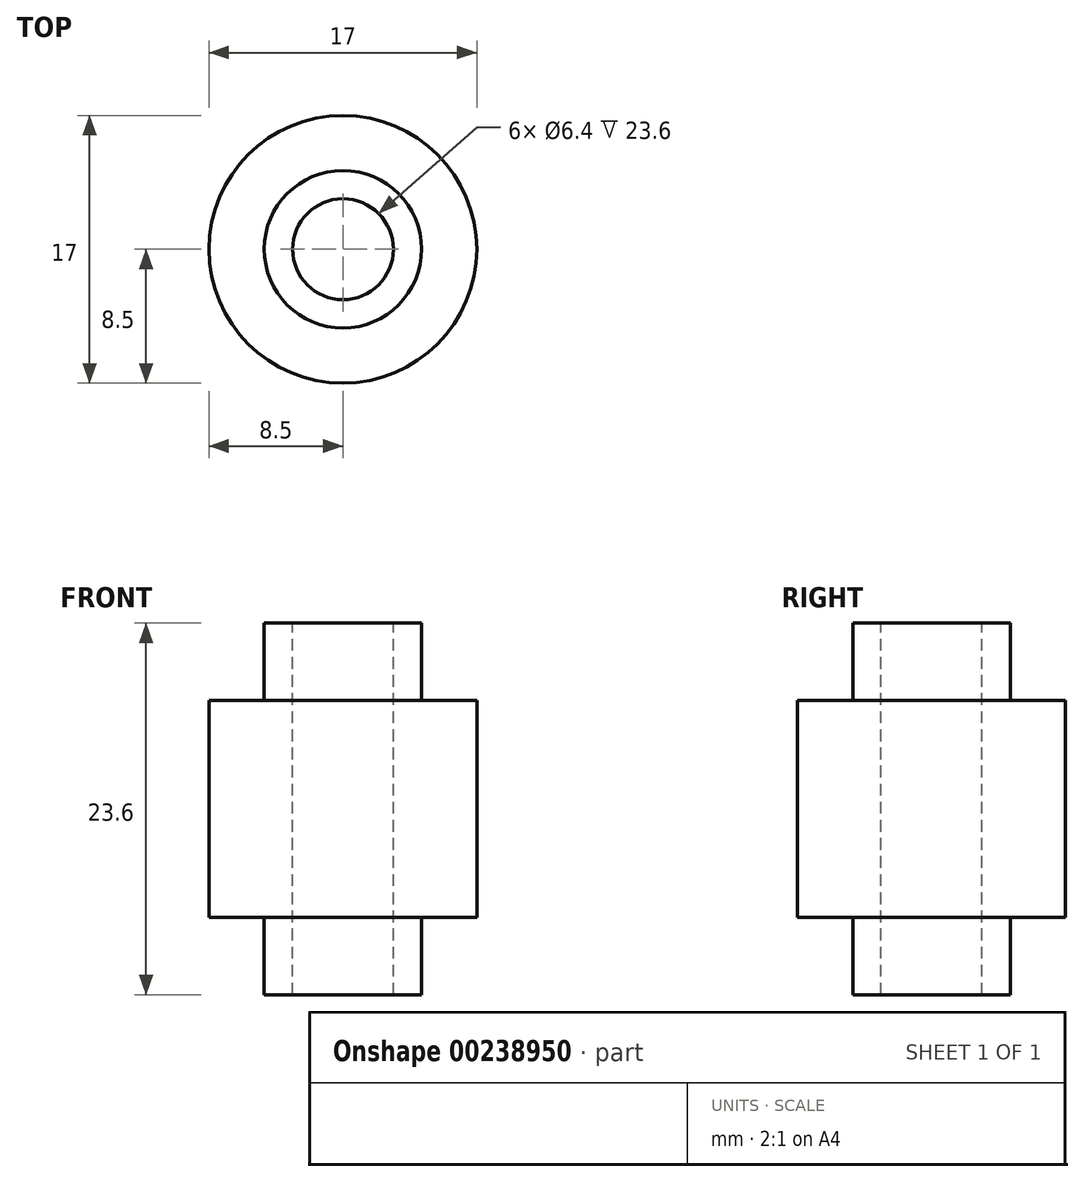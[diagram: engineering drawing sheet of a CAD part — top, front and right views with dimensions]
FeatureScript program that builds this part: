
annotation { "Feature Type Name" : "Feature", "Feature Type Description" : "" }
export const myFeature = defineFeature(function(context is Context, id is Id, definition is map)
    precondition{}
    {
        {
            var Q0;
            Q0=qCreatedBy(makeId("Front.planeOp"),FACE);
            var sketch = newSketch(context, id + "F0", { "sketchPlane" : qUnion([Q0])});
            skLineSegment(sketch, "E0", {"start": v(0, 11.8) * mm, "end": v(5, 11.8) * mm});
            skLineSegment(sketch, "E1", {"start": v(5, 11.8) * mm, "end": v(5, 6.9) * mm});
            skLineSegment(sketch, "E2", {"start": v(5, 6.9) * mm, "end": v(8.5, 6.9) * mm});
            skLineSegment(sketch, "E3", {"start": v(8.5, 6.9) * mm, "end": v(8.5, 0) * mm});
            skLineSegment(sketch, "E4", {"start": v(0, 25.28) * mm, "end": v(0, -24.24) * mm});
            skLineSegment(sketch, "E5.MirrorCS", {"start": v(5, -6.9) * mm, "end": v(8.5, -6.9) * mm});
            skLineSegment(sketch, "E6.MirrorCS", {"start": v(0, -11.8) * mm, "end": v(5, -11.8) * mm});
            skLineSegment(sketch, "E7.MirrorCS", {"start": v(8.5, -6.9) * mm, "end": v(8.5, 0) * mm});
            skLineSegment(sketch, "E8.MirrorCS", {"start": v(5, -11.8) * mm, "end": v(5, -6.9) * mm});
            skSolve(sketch);
        }
        {
            var Q0;
            {var subQ0=sQuery(id+"F0.wireOp",EDGE,"E0");Q0=makeQuery(id+"F0.imprint","IMPRINT",FACE,{"disambiguationData":[TD([[makeQuery(id+"F0.imprint","IMPRINT",EDGE,{"derivedFrom":subQ0}),-1.0]])]});}
            var Q1;
            Q1=sQuery(id+"F0.wireOp",EDGE,"E4");
            revolve(context, id + "F1", {"entities" : qUnion([Q0]), "axis" : qUnion([Q1]), "revolveType" : RevolveType.FULL});
        }
        {
            var Q0;
            Q0=makeQuery(id+"F1.opRevolve","SWEPT_FACE",FACE,{"disambiguationData":[OSD([sQuery(id+"F0.wireOp",EDGE,"E0")])]});
            var sketch = newSketch(context, id + "F2", { "sketchPlane" : qUnion([Q0])});
            skCircle(sketch, "E9.0", {"center": v(0, 0) * mm, "radius": 5 * mm, "construction": true});
            skSolve(sketch);
        }
        {
            var Q0;
            Q0=sQuery(id+"F2.wireOp",VERTEX,"E9.0.center");
            var Q1;
            Q1=makeQuery(id+"F1.opRevolve","SWEPT_BODY",BODY,{"disambiguationData":[OSD([sQuery(id+"F0.wireOp",EDGE,"E0"),sQuery(id+"F0.wireOp",EDGE,"E1"),sQuery(id+"F0.wireOp",EDGE,"E2"),sQuery(id+"F0.wireOp",EDGE,"E3"),sQuery(id+"F0.wireOp",EDGE,"E4"),sQuery(id+"F0.wireOp",EDGE,"E5.MirrorCS"),sQuery(id+"F0.wireOp",EDGE,"E6.MirrorCS"),sQuery(id+"F0.wireOp",EDGE,"E7.MirrorCS"),sQuery(id+"F0.wireOp",EDGE,"E8.MirrorCS")])]});
            hole(context, id + "F3", {"style" : HoleStyle.SIMPLE, "endStyle" : HoleEndStyle.THROUGH, "holeDiameter" : 6.4 * mm, "locations" : qUnion([Q0]), "scope" : qUnion([Q1]), "isTappedThrough" : true});
        }
    });
